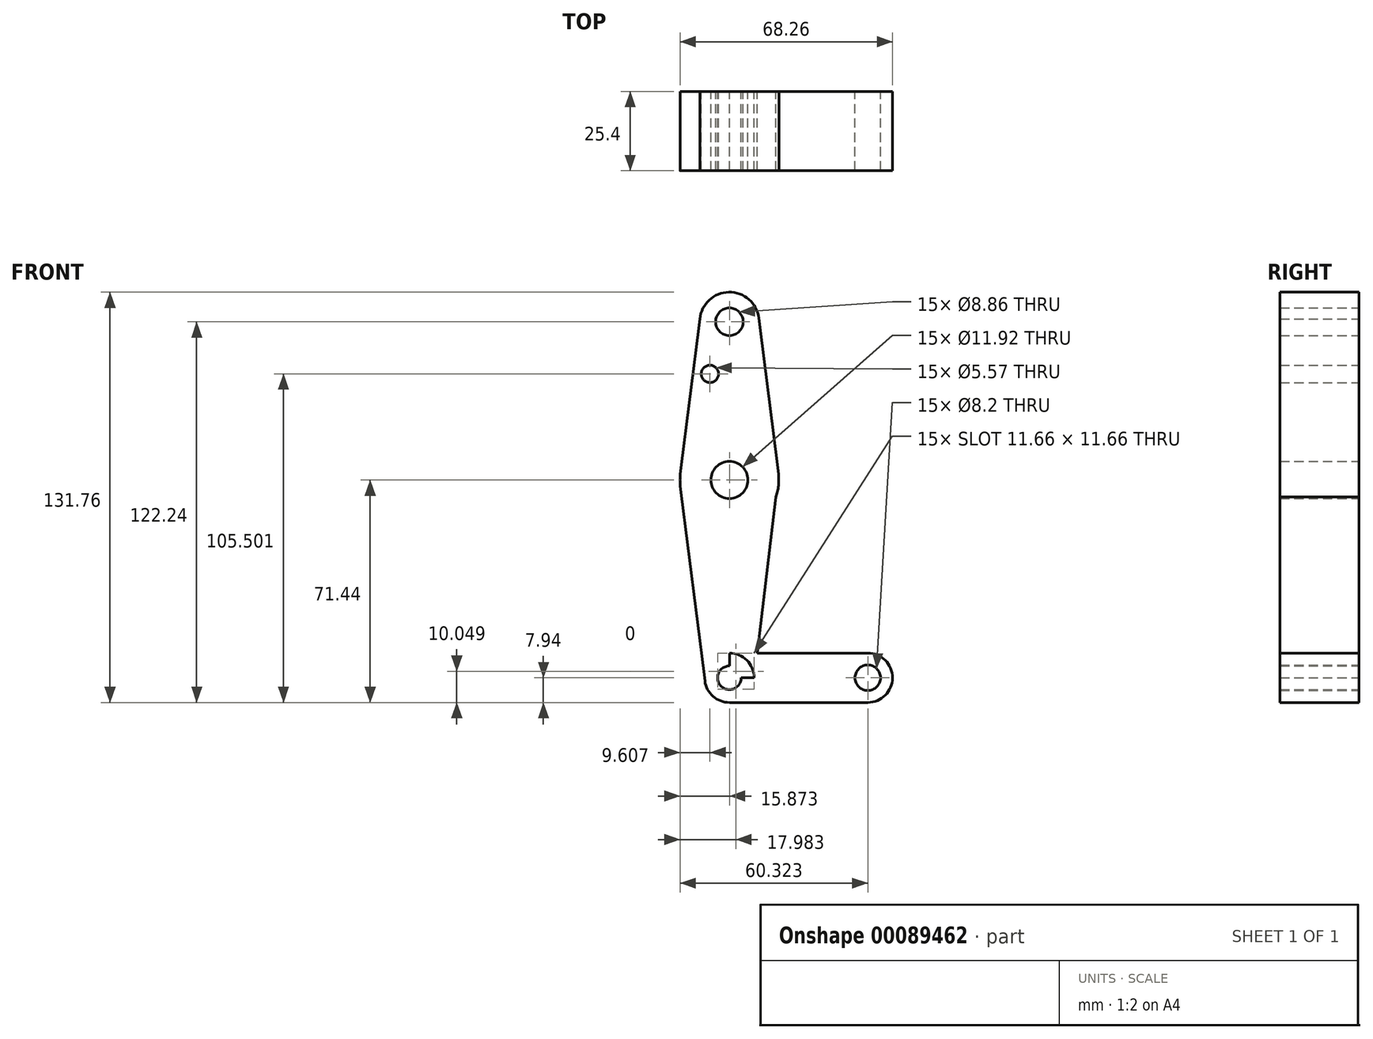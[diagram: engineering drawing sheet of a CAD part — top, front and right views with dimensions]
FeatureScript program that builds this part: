
annotation { "Feature Type Name" : "Feature", "Feature Type Description" : "" }
export const myFeature = defineFeature(function(context is Context, id is Id, definition is map)
    precondition{}
    {
        {
            var Q0;
            Q0=qCreatedBy(makeId("Front.planeOp"),FACE);
            var sketch = newSketch(context, id + "F0", { "sketchPlane" : qUnion([Q0])});
            skLineSegment(sketch, "E0", {"start": v(-176.92, 114.3) * mm, "end": v(-176.92, 63.5) * mm});
            skLineSegment(sketch, "E1", {"start": v(-176.92, 63.5) * mm, "end": v(-176.92, 0) * mm});
            skLineSegment(sketch, "E2", {"start": v(-176.92, 0) * mm, "end": v(-132.47, 0) * mm});
            skCircle(sketch, "E3", {"center": v(-176.92, 114.3) * mm, "radius": 9.53 * mm});
            skCircle(sketch, "E4", {"center": v(-176.92, 63.5) * mm, "radius": 15.88 * mm});
            skCircle(sketch, "E5", {"center": v(-176.92, 0) * mm, "radius": 7.94 * mm});
            skCircle(sketch, "E6", {"center": v(-132.47, 0) * mm, "radius": 7.94 * mm});
            skLineSegment(sketch, "E7", {"start": v(-186.33, 115.78) * mm, "end": v(-192.67, 65.49) * mm});
            skLineSegment(sketch, "E8", {"start": v(-161.15, 65.34) * mm, "end": v(-168.92, 0) * mm});
            skLineSegment(sketch, "E9", {"start": v(-176.92, 7.94) * mm, "end": v(-132.47, 7.94) * mm});
            skLineSegment(sketch, "E10", {"start": v(-132.47, 7.94) * mm, "end": v(-132.47, -7.94) * mm});
            skLineSegment(sketch, "E11", {"start": v(-132.47, -7.94) * mm, "end": v(-176.92, -7.94) * mm});
            skCircle(sketch, "E12", {"center": v(-176.92, 0) * mm, "radius": 3.8 * mm});
            skCircle(sketch, "E13", {"center": v(-132.47, 0) * mm, "radius": 4.1 * mm});
            skCircle(sketch, "E14", {"center": v(-176.92, 63.5) * mm, "radius": 5.96 * mm});
            skCircle(sketch, "E15", {"center": v(-176.92, 114.3) * mm, "radius": 4.43 * mm});
            skCircle(sketch, "E16", {"center": v(-183.18, 97.56) * mm, "radius": 2.78 * mm});
            skLineSegment(sketch, "E17", {"start": v(-167.47, 115.5) * mm, "end": v(-161.17, 65.48) * mm});
            skLineSegment(sketch, "E18", {"start": v(-192.67, 61.52) * mm, "end": v(-184.8, -1) * mm});
            skSolve(sketch);
        }
        {
            var Q0;
            Q0 = qSketchRegion(id + "F0", true);
            extrude(context, id + "F1", {"entities" : qUnion([Q0]), "depth" : 25.4 * mm});
        }
    });
